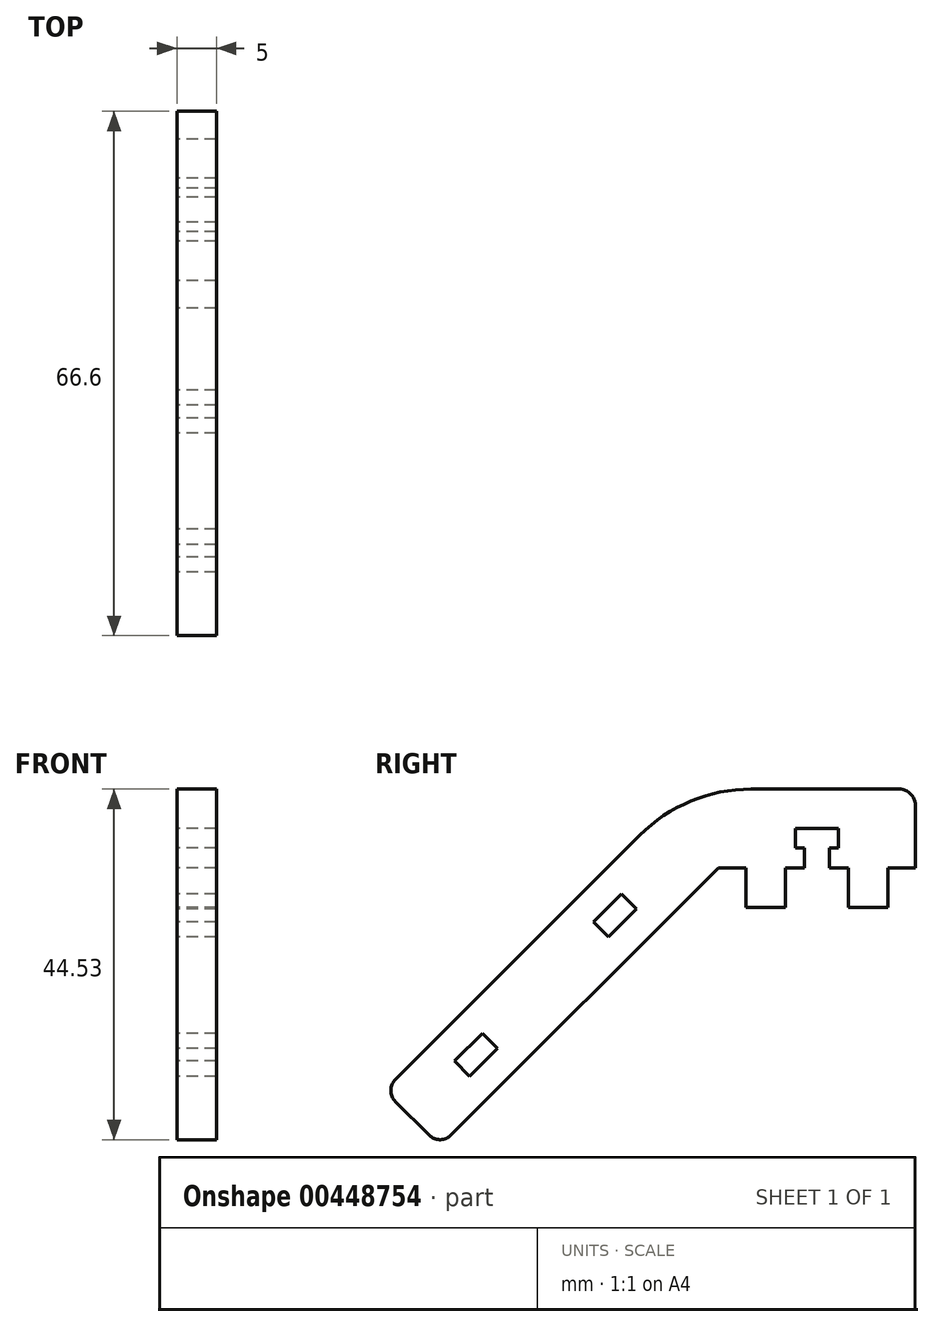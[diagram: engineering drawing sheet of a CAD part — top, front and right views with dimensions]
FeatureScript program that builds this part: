
annotation { "Feature Type Name" : "Feature", "Feature Type Description" : "" }
export const myFeature = defineFeature(function(context is Context, id is Id, definition is map)
    precondition{}
    {
        {
            assignVariable(context, id + "F0", {"name" : "thickness", "anyValue" : 5 * mm});
        }
        {
            var Q0;
            Q0=qCreatedBy(makeId("Right.planeOp"),FACE);
            var sketch = newSketch(context, id + "F1", { "sketchPlane" : qUnion([Q0])});
            skLineSegment(sketch, "E0", {"start": v(0, 0) * mm, "end": v(-10.9, 0) * mm});
            skLineSegment(sketch, "E1", {"start": v(-25, 0) * mm, "end": v(-58.94, -33.94) * mm});
            skLineSegment(sketch, "E2", {"start": v(0, 0) * mm, "end": v(0, 8) * mm});
            skLineSegment(sketch, "E3", {"start": v(-2, 10) * mm, "end": v(-20.86, 10) * mm});
            skLineSegment(sketch, "E4", {"start": v(-35, 4.14) * mm, "end": v(-66.01, -26.87) * mm});
            skLineSegment(sketch, "E5", {"start": v(-66.01, -29.7) * mm, "end": v(-61.77, -33.94) * mm});
            skLineSegment(sketch, "E6", {"start": v(-3.5, 0) * mm, "end": v(-3.5, -5) * mm});
            skLineSegment(sketch, "E7", {"start": v(-3.5, -5) * mm, "end": v(-8.5, -5) * mm});
            skLineSegment(sketch, "E8", {"start": v(-8.5, -5) * mm, "end": v(-8.5, 0) * mm});
            skLineSegment(sketch, "E9", {"start": v(-16.5, 0) * mm, "end": v(-16.5, -5) * mm});
            skLineSegment(sketch, "E10", {"start": v(-16.5, -5) * mm, "end": v(-21.5, -5) * mm});
            skLineSegment(sketch, "E11", {"start": v(-21.5, -5) * mm, "end": v(-21.5, 0) * mm});
            skLineSegment(sketch, "E12", {"start": v(-12.5, 0) * mm, "end": v(-12.5, 10) * mm, "construction": true});
            skLineSegment(sketch, "E13", {"start": v(-14.1, 0) * mm, "end": v(-14.1, 2.5) * mm});
            skLineSegment(sketch, "E14", {"start": v(-14.1, 2.5) * mm, "end": v(-15.25, 2.5) * mm});
            skLineSegment(sketch, "E15", {"start": v(-15.25, 2.5) * mm, "end": v(-15.25, 5) * mm});
            skLineSegment(sketch, "E16", {"start": v(-15.25, 5) * mm, "end": v(-12.5, 5) * mm});
            skLineSegment(sketch, "E17.MirrorCS", {"start": v(-9.75, 5) * mm, "end": v(-12.5, 5) * mm});
            skLineSegment(sketch, "E18.MirrorCS", {"start": v(-9.75, 2.5) * mm, "end": v(-9.75, 5) * mm});
            skLineSegment(sketch, "E19.MirrorCS", {"start": v(-10.9, 2.5) * mm, "end": v(-9.75, 2.5) * mm});
            skLineSegment(sketch, "E20.MirrorCS", {"start": v(-10.9, 0) * mm, "end": v(-10.9, 2.5) * mm});
            skLineSegment(sketch, "E21.trimOffspring", {"start": v(-14.1, 0) * mm, "end": v(-25, 0) * mm});
            skPoint(sketch, "E22.visualSharp", {"position": v(-29.14, 10) * mm});
            skArc(sketch, "E22.filletArc", {"start": v(-20.86, 10) * mm, "mid": v(-28.51, 8.48) * mm, "end": v(-35, 4.14) * mm});
            skPoint(sketch, "E23.visualSharp", {"position": v(-67.43, -28.28) * mm});
            skArc(sketch, "E23.filletArc", {"start": v(-66.01, -26.87) * mm, "mid": v(-66.6, -28.28) * mm, "end": v(-66.01, -29.7) * mm});
            skPoint(sketch, "E24.visualSharp", {"position": v(-60.36, -35.36) * mm});
            skArc(sketch, "E24.filletArc", {"start": v(-61.77, -33.94) * mm, "mid": v(-60.36, -34.53) * mm, "end": v(-58.94, -33.94) * mm});
            skPoint(sketch, "E25.visualSharp", {"position": v(0, 10) * mm});
            skArc(sketch, "E25.filletArc", {"start": v(0, 8) * mm, "mid": v(-0.59, 9.41) * mm, "end": v(-2, 10) * mm});
            skLineSegment(sketch, "E26", {"start": v(-37.32, -3.34) * mm, "end": v(-40.85, -6.87) * mm});
            skLineSegment(sketch, "E27", {"start": v(-40.85, -6.87) * mm, "end": v(-38.94, -8.78) * mm});
            skLineSegment(sketch, "E28", {"start": v(-38.94, -8.78) * mm, "end": v(-35.4, -5.25) * mm});
            skLineSegment(sketch, "E29", {"start": v(-35.4, -5.25) * mm, "end": v(-37.32, -3.34) * mm});
            skLineSegment(sketch, "E30", {"start": v(-50.5, -11.36) * mm, "end": v(-43.44, -18.44) * mm, "construction": true});
            skLineSegment(sketch, "E31", {"start": v(-39.14, 0) * mm, "end": v(-32.07, -7.07) * mm, "construction": true});
            skLineSegment(sketch, "E32.MirrorCS", {"start": v(-58.53, -24.55) * mm, "end": v(-55, -21.02) * mm});
            skLineSegment(sketch, "E33.MirrorCS", {"start": v(-55, -21.02) * mm, "end": v(-53.09, -22.93) * mm});
            skLineSegment(sketch, "E34.MirrorCS", {"start": v(-53.09, -22.93) * mm, "end": v(-56.62, -26.46) * mm});
            skLineSegment(sketch, "E35.MirrorCS", {"start": v(-56.62, -26.46) * mm, "end": v(-58.53, -24.55) * mm});
            skLineSegment(sketch, "E36", {"start": v(-63.9, -31.82) * mm, "end": v(-35.6, -3.54) * mm, "construction": true});
            skPoint(sketch, "E37", {"position": v(-57.58, -25.5) * mm});
            skSolve(sketch);
        }
        {
            var Q0;
            Q0=qSketchRegion(id+"F1",true);
            extrude(context, id + "F2", {"entities" : qUnion([Q0]), "depth" : getVariable(context, 'thickness')});
        }
    });
